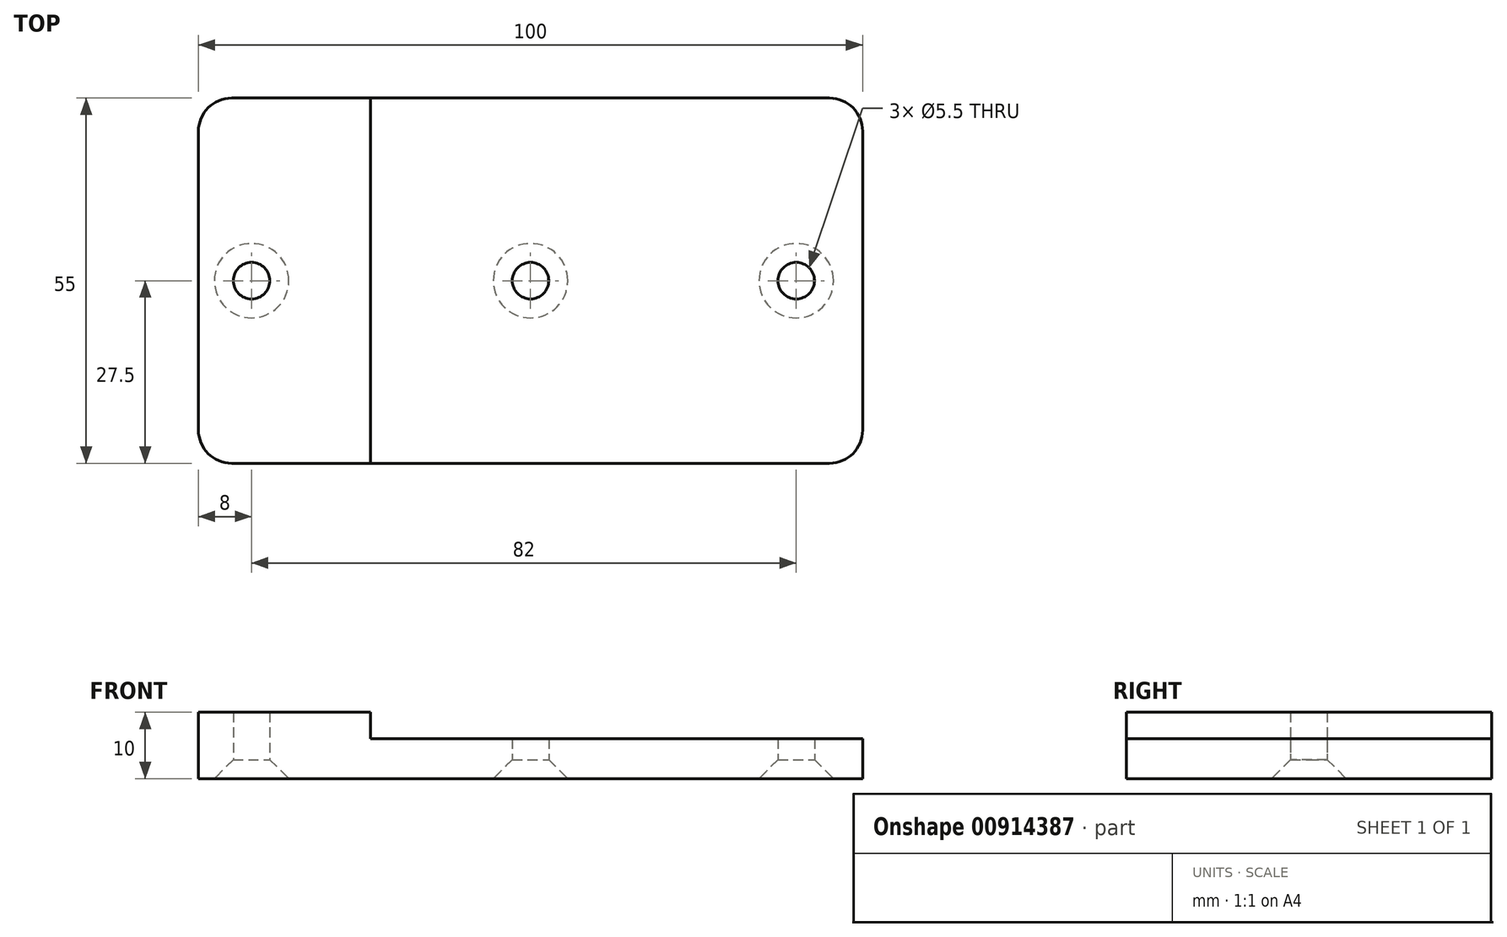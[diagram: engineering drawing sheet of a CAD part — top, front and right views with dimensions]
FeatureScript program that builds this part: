
annotation { "Feature Type Name" : "Feature", "Feature Type Description" : "" }
export const myFeature = defineFeature(function(context is Context, id is Id, definition is map)
    precondition{}
    {
        {
            var Q0;
            Q0=qCreatedBy(makeId("Top.planeOp"),FACE);
            var sketch = newSketch(context, id + "F0", { "sketchPlane" : qUnion([Q0])});
            skLineSegment(sketch, "E0.bottom", {"start": v(45, -27.5) * mm, "end": v(-45, -27.5) * mm});
            skLineSegment(sketch, "E0.top", {"start": v(45, 27.5) * mm, "end": v(-45, 27.5) * mm});
            skLineSegment(sketch, "E0.left", {"start": v(50, -22.5) * mm, "end": v(50, 22.5) * mm});
            skLineSegment(sketch, "E0.right", {"start": v(-50, -22.5) * mm, "end": v(-50, 22.5) * mm});
            skPoint(sketch, "E0.middle", {"position": v(0, 0) * mm});
            skPoint(sketch, "E1.visualSharp", {"position": v(50, 27.5) * mm});
            skArc(sketch, "E1.filletArc", {"start": v(50, 22.5) * mm, "mid": v(48.54, 26.04) * mm, "end": v(45, 27.5) * mm});
            skPoint(sketch, "E2.visualSharp", {"position": v(-50, 27.5) * mm});
            skArc(sketch, "E2.filletArc", {"start": v(-45, 27.5) * mm, "mid": v(-48.54, 26.04) * mm, "end": v(-50, 22.5) * mm});
            skPoint(sketch, "E3.visualSharp", {"position": v(-50, -27.5) * mm});
            skArc(sketch, "E3.filletArc", {"start": v(-50, -22.5) * mm, "mid": v(-48.54, -26.04) * mm, "end": v(-45, -27.5) * mm});
            skPoint(sketch, "E4.visualSharp", {"position": v(50, -27.5) * mm});
            skArc(sketch, "E4.filletArc", {"start": v(45, -27.5) * mm, "mid": v(48.54, -26.04) * mm, "end": v(50, -22.5) * mm});
            skLineSegment(sketch, "E5", {"start": v(86.6, 0) * mm, "end": v(-90.1, 0) * mm, "construction": true});
            skLineSegment(sketch, "E6", {"start": v(50, 72.45) * mm, "end": v(50, -75.94) * mm, "construction": true});
            skLineSegment(sketch, "E7", {"start": v(40, 72.45) * mm, "end": v(40, -75.94) * mm, "construction": true});
            skPoint(sketch, "E8", {"position": v(40, 0) * mm});
            skPoint(sketch, "E9", {"position": v(-1, 0) * mm});
            skPoint(sketch, "E10", {"position": v(-42, 0) * mm});
            skSolve(sketch);
        }
        {
            var Q0;
            Q0=makeQuery(id+"F0.imprint","IMPRINT",FACE,{"disambiguationData":[TD([[makeQuery(id+"F0.imprint","IMPRINT",EDGE,{"derivedFrom":sQuery(id+"F0.wireOp",EDGE,"E0.bottom")}),-1.0]])]});
            extrude(context, id + "F1", {"entities" : qUnion([Q0]), "depth" : 6 * mm, "offsetDistance" : 25 * mm});
        }
        {
            var Q0;
            Q0=sQuery(id+"F0.wireOp",VERTEX,"E8");
            var Q1;
            Q1=sQuery(id+"F0.wireOp",VERTEX,"E0.middle");
            var Q2;
            Q2=sQuery(id+"F0.wireOp",VERTEX,"E10");
            var Q3;
            Q3=makeQuery(id+"F1.opExtrude","SWEPT_BODY",BODY,{"disambiguationData":[OSD([sQuery(id+"F0.wireOp",EDGE,"E0.bottom"),sQuery(id+"F0.wireOp",EDGE,"E0.top"),sQuery(id+"F0.wireOp",EDGE,"E0.left"),sQuery(id+"F0.wireOp",EDGE,"E0.right"),sQuery(id+"F0.wireOp",EDGE,"E1.filletArc"),sQuery(id+"F0.wireOp",EDGE,"E2.filletArc"),sQuery(id+"F0.wireOp",EDGE,"E3.filletArc"),sQuery(id+"F0.wireOp",EDGE,"E4.filletArc")])]});
            hole(context, id + "F2", {"style" : HoleStyle.C_SINK, "endStyle" : HoleEndStyle.THROUGH, "oppositeDirection" : true, "standardTappedOrClearance" : lookupTablePath({ "fit" : "Standard", "standard" : "ISO", "size" : "M5", "type" : "Clearance" }), "standardBlindInLast" : lookupTablePath({ "fit" : "Standard", "standard" : "ISO", "size" : "M5", "type" : "Clearance" }), "holeDiameter" : 5.5 * mm, "cSinkDiameter" : 11.2 * mm, "cSinkAngle" : 90 * degree, "majorDiameter" : 5 * mm, "isTappedThrough" : true, "tappedDepth" : 8 * mm, "tapClearance" : 3, "locations" : qUnion([Q0, Q1, Q2]), "scope" : qUnion([Q3])});
        }
        {
            var Q0;
            Q0=makeQuery(id+"F1.opExtrude","CAP_FACE",FACE,{"disambiguationData":[OSD([sQuery(id+"F0.wireOp",EDGE,"E0.bottom"),sQuery(id+"F0.wireOp",EDGE,"E0.top"),sQuery(id+"F0.wireOp",EDGE,"E0.left"),sQuery(id+"F0.wireOp",EDGE,"E0.right"),sQuery(id+"F0.wireOp",EDGE,"E1.filletArc"),sQuery(id+"F0.wireOp",EDGE,"E2.filletArc"),sQuery(id+"F0.wireOp",EDGE,"E3.filletArc"),sQuery(id+"F0.wireOp",EDGE,"E4.filletArc")])],"isStart":false});
            var sketch = newSketch(context, id + "F3", { "sketchPlane" : qUnion([Q0])});
            skLineSegment(sketch, "E11.0", {"start": v(-50, -22.5) * mm, "end": v(-50, 22.5) * mm});
            skPoint(sketch, "E12.0", {"position": v(-48.54, 26.04) * mm});
            skPoint(sketch, "E13.0", {"position": v(-48.54, -26.04) * mm});
            skLineSegment(sketch, "E14", {"start": v(-24.1, 27.5) * mm, "end": v(-24.1, -27.5) * mm});
            skArc(sketch, "E15.0", {"start": v(-50, -22.5) * mm, "mid": v(-48.54, -26.04) * mm, "end": v(-45, -27.5) * mm});
            skArc(sketch, "E16.0", {"start": v(-45, 27.5) * mm, "mid": v(-48.54, 26.04) * mm, "end": v(-50, 22.5) * mm});
            skLineSegment(sketch, "E17", {"start": v(-24.1, 27.5) * mm, "end": v(-45, 27.5) * mm});
            skLineSegment(sketch, "E18", {"start": v(-24.1, -27.5) * mm, "end": v(-45, -27.5) * mm});
            skSolve(sketch);
        }
        {
            var Q0;
            Q0=makeQuery(id+"F3.imprint","IMPRINT",FACE,{"disambiguationData":[TD([[makeQuery(id+"F3.imprint","IMPRINT",EDGE,{"derivedFrom":sQuery(id+"F3.wireOp",EDGE,"E11.0")}),-1.0]])]});
            extrude(context, id + "F4", {"entities" : qUnion([Q0]), "operationType" : NewBodyOperationType.ADD, "depth" : 4 * mm, "offsetDistance" : 25 * mm});
        }
    });
